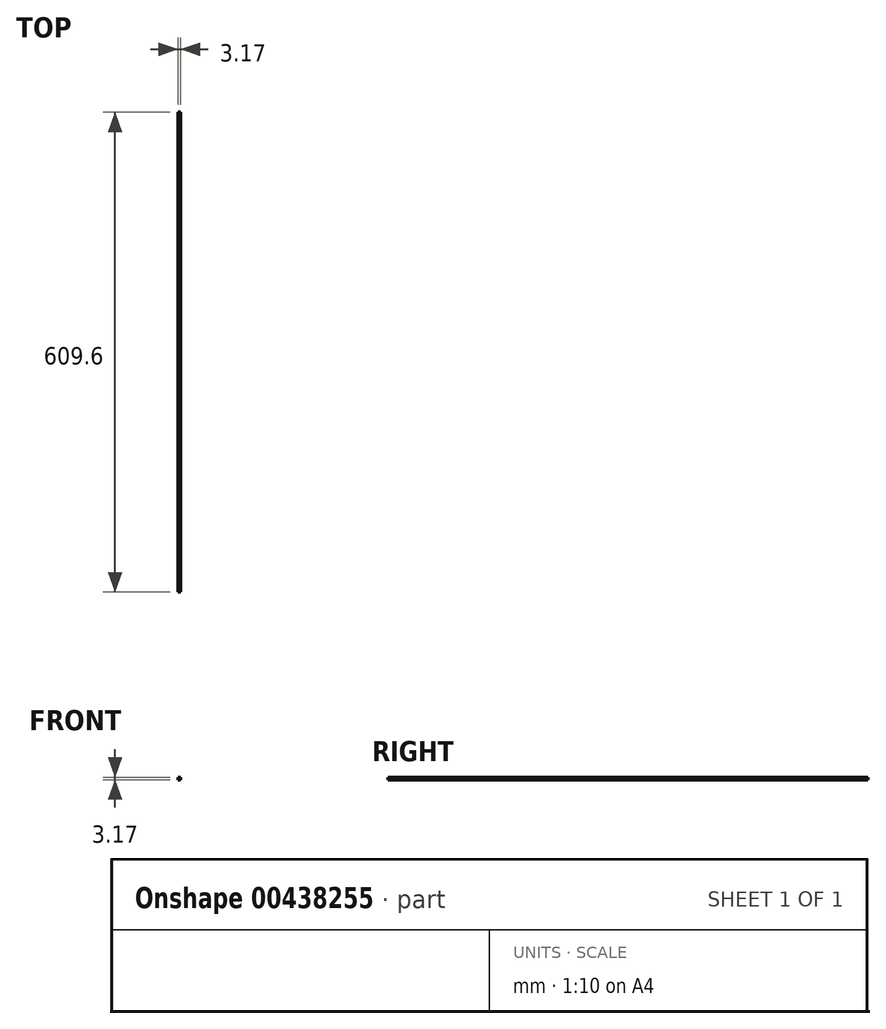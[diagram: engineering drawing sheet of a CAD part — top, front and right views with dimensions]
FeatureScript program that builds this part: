
annotation { "Feature Type Name" : "Feature", "Feature Type Description" : "" }
export const myFeature = defineFeature(function(context is Context, id is Id, definition is map)
    precondition{}
    {
        {
            var Q0;
            Q0=qCreatedBy(makeId("Front.planeOp"),FACE);
            var sketch = newSketch(context, id + "F0", { "sketchPlane" : qUnion([Q0])});
            skLineSegment(sketch, "E0.bottom", {"start": v(-39.33, 15.52) * mm, "end": v(-36.16, 15.52) * mm});
            skLineSegment(sketch, "E0.top", {"start": v(-39.33, 12.35) * mm, "end": v(-36.16, 12.35) * mm});
            skLineSegment(sketch, "E0.left", {"start": v(-39.33, 15.52) * mm, "end": v(-39.33, 12.35) * mm});
            skLineSegment(sketch, "E0.right", {"start": v(-36.16, 15.52) * mm, "end": v(-36.16, 12.35) * mm});
            skSolve(sketch);
        }
        {
            var Q0;
            Q0 = qSketchRegion(id + "F0", true);
            extrude(context, id + "F1", {"entities" : qUnion([Q0]), "depth" : 609.6 * mm});
        }
    });
